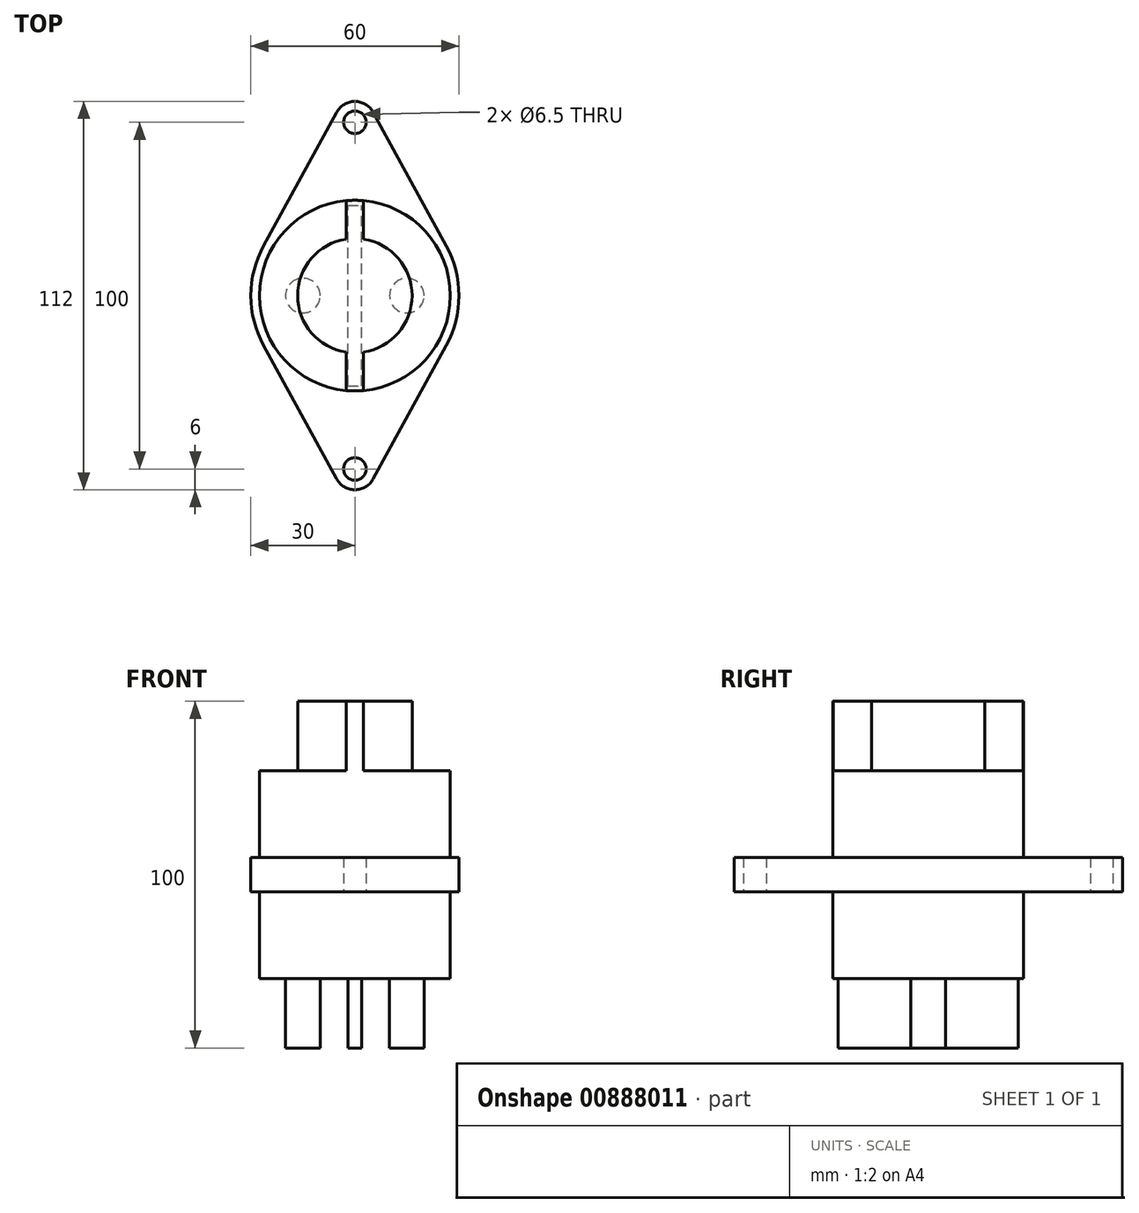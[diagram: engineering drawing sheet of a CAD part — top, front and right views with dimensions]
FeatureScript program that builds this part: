
annotation { "Feature Type Name" : "Feature", "Feature Type Description" : "" }
export const myFeature = defineFeature(function(context is Context, id is Id, definition is map)
    precondition{}
    {
        {
            var Q0;
            Q0=qCreatedBy(makeId("Top.planeOp"),FACE);
            var sketch = newSketch(context, id + "F0", { "sketchPlane" : qUnion([Q0])});
            skCircle(sketch, "E0", {"center": v(0, 0) * mm, "radius": 30 * mm});
            skCircle(sketch, "E1", {"center": v(0, 50) * mm, "radius": 3.25 * mm});
            skCircle(sketch, "E2.MirrorC", {"center": v(0, -50) * mm, "radius": 3.25 * mm});
            skCircle(sketch, "E3", {"center": v(0, 50) * mm, "radius": 6 * mm});
            skCircle(sketch, "E4.MirrorC", {"center": v(0, -50) * mm, "radius": 6 * mm});
            skLineSegment(sketch, "E5", {"start": v(-26.44, 14.18) * mm, "end": v(-5.26, 52.88) * mm});
            skLineSegment(sketch, "E6.MirrorCS", {"start": v(26.44, 14.18) * mm, "end": v(5.26, 52.88) * mm});
            skLineSegment(sketch, "E7.MirrorCS", {"start": v(-26.44, -14.18) * mm, "end": v(-5.26, -52.88) * mm});
            skLineSegment(sketch, "E8.MirrorCS", {"start": v(26.44, -14.18) * mm, "end": v(5.26, -52.88) * mm});
            skSolve(sketch);
        }
        {
            var Q0;
            Q0 = qSketchRegion(id + "F0", true);
            extrude(context, id + "F1", {"entities" : qUnion([Q0]), "endBound" : BoundingType.SYMMETRIC, "depth" : 100 * mm, "offsetDistance" : 25 * mm});
        }
        {
            var Q0;
            Q0=makeQuery(id+"F1.opExtrude","CAP_FACE",FACE,{"disambiguationData":[OSD([sQuery(id+"F0.wireOp",EDGE,"E0"),sQuery(id+"F0.wireOp",EDGE,"E1"),sQuery(id+"F0.wireOp",EDGE,"E2.MirrorC"),sQuery(id+"F0.wireOp",EDGE,"E3"),sQuery(id+"F0.wireOp",EDGE,"E4.MirrorC"),sQuery(id+"F0.wireOp",EDGE,"E5"),sQuery(id+"F0.wireOp",EDGE,"E6.MirrorCS"),sQuery(id+"F0.wireOp",EDGE,"E7.MirrorCS"),sQuery(id+"F0.wireOp",EDGE,"E8.MirrorCS")])],"isStart":false});
            var sketch = newSketch(context, id + "F2", { "sketchPlane" : qUnion([Q0])});
            skCircle(sketch, "E9", {"center": v(0, 0) * mm, "radius": 27.5 * mm});
            skLineSegment(sketch, "E10.bottom", {"start": v(-55.61, 69.95) * mm, "end": v(65.23, 69.95) * mm});
            skLineSegment(sketch, "E10.top", {"start": v(-55.61, -69.95) * mm, "end": v(65.23, -69.95) * mm});
            skLineSegment(sketch, "E10.left", {"start": v(-55.61, 69.95) * mm, "end": v(-55.61, -69.95) * mm});
            skLineSegment(sketch, "E10.right", {"start": v(65.23, 69.95) * mm, "end": v(65.23, -69.95) * mm});
            skSolve(sketch);
        }
        {
            var Q0;
            Q0 = qSketchRegion(id + "F2", true);
            extrude(context, id + "F3", {"entities" : qUnion([Q0]), "operationType" : NewBodyOperationType.REMOVE, "oppositeDirection" : true, "depth" : 45 * mm, "offsetDistance" : 25 * mm});
        }
        {
            var Q0;
            Q0=makeQuery(id+"F1.opExtrude","CAP_FACE",FACE,{"disambiguationData":[OSD([sQuery(id+"F0.wireOp",EDGE,"E0"),sQuery(id+"F0.wireOp",EDGE,"E1"),sQuery(id+"F0.wireOp",EDGE,"E2.MirrorC"),sQuery(id+"F0.wireOp",EDGE,"E3"),sQuery(id+"F0.wireOp",EDGE,"E4.MirrorC"),sQuery(id+"F0.wireOp",EDGE,"E5"),sQuery(id+"F0.wireOp",EDGE,"E6.MirrorCS"),sQuery(id+"F0.wireOp",EDGE,"E7.MirrorCS"),sQuery(id+"F0.wireOp",EDGE,"E8.MirrorCS")])],"isStart":false});
            var sketch = newSketch(context, id + "F4", { "sketchPlane" : qUnion([Q0])});
            skArc(sketch, "E11", {"start": v(-2.5, 38.39) * mm, "mid": v(-38.47, 0) * mm, "end": v(-2.5, -38.39) * mm});
            skArc(sketch, "E12", {"start": v(-2.5, 16.31) * mm, "mid": v(-16.5, 0) * mm, "end": v(-2.5, -16.31) * mm});
            skLineSegment(sketch, "E13.0", {"start": v(-2.5, 38.39) * mm, "end": v(-2.5, 16.31) * mm});
            skLineSegment(sketch, "E14.0", {"start": v(2.5, 38.39) * mm, "end": v(2.5, 16.31) * mm});
            skPoint(sketch, "E15.start.orphan", {"position": v(0, 38.47) * mm});
            skLineSegment(sketch, "E16.MirrorCS", {"start": v(-2.5, -38.39) * mm, "end": v(-2.5, -16.31) * mm});
            skLineSegment(sketch, "E17.MirrorCS", {"start": v(2.5, -38.39) * mm, "end": v(2.5, -16.31) * mm});
            skArc(sketch, "E18.trimOffspring", {"start": v(2.5, -16.31) * mm, "mid": v(16.5, 0) * mm, "end": v(2.5, 16.31) * mm});
            skArc(sketch, "E19.trimOffspring", {"start": v(2.5, -38.39) * mm, "mid": v(38.47, 0) * mm, "end": v(2.5, 38.39) * mm});
            skSolve(sketch);
        }
        {
            var Q0;
            Q0 = qSketchRegion(id + "F4", true);
            extrude(context, id + "F5", {"entities" : qUnion([Q0]), "operationType" : NewBodyOperationType.REMOVE, "oppositeDirection" : true, "depth" : 20 * mm, "offsetDistance" : 25 * mm});
        }
        {
            var Q0;
            Q0=makeQuery(id+"F1.opExtrude","CAP_FACE",FACE,{"disambiguationData":[OSD([sQuery(id+"F0.wireOp",EDGE,"E0"),sQuery(id+"F0.wireOp",EDGE,"E1"),sQuery(id+"F0.wireOp",EDGE,"E2.MirrorC"),sQuery(id+"F0.wireOp",EDGE,"E3"),sQuery(id+"F0.wireOp",EDGE,"E4.MirrorC"),sQuery(id+"F0.wireOp",EDGE,"E5"),sQuery(id+"F0.wireOp",EDGE,"E6.MirrorCS"),sQuery(id+"F0.wireOp",EDGE,"E7.MirrorCS"),sQuery(id+"F0.wireOp",EDGE,"E8.MirrorCS")])],"isStart":false});
            var sketch = newSketch(context, id + "F6", { "sketchPlane" : qUnion([Q0])});
            skCircle(sketch, "E20", {"center": v(0, 0) * mm, "radius": 6 * mm});
            skArc(sketch, "E21", {"start": v(2.5, -22.15) * mm, "mid": v(22.3, 0) * mm, "end": v(2.5, 22.15) * mm});
            skLineSegment(sketch, "E22", {"start": v(-2.5, 22.15) * mm, "end": v(-2.5, 5.45) * mm});
            skLineSegment(sketch, "E23", {"start": v(2.5, 22.15) * mm, "end": v(2.5, 5.45) * mm});
            skLineSegment(sketch, "E24.MirrorCS", {"start": v(-2.5, -22.15) * mm, "end": v(-2.5, -5.45) * mm});
            skLineSegment(sketch, "E25.MirrorCS", {"start": v(2.5, -22.15) * mm, "end": v(2.5, -5.45) * mm});
            skPoint(sketch, "E26.orphan", {"position": v(-2.5, 23.79) * mm});
            skPoint(sketch, "E27.orphan", {"position": v(2.5, 23.71) * mm});
            skPoint(sketch, "E28.orphan", {"position": v(-2.5, -23.79) * mm});
            skPoint(sketch, "E29.orphan", {"position": v(2.5, -23.71) * mm});
            skArc(sketch, "E30.trimOffspring", {"start": v(-2.5, 22.15) * mm, "mid": v(-22.3, 0) * mm, "end": v(-2.5, -22.15) * mm});
            skSolve(sketch);
        }
        {
            var Q0;
            {var subQ0=sQuery(id+"F6.wireOp",EDGE,"E21");Q0=makeQuery(id+"F6.imprint","IMPRINT",FACE,{"disambiguationData":[TD([[makeQuery(id+"F6.imprint","IMPRINT",EDGE,{"derivedFrom":subQ0}),1.0]])]});}
            var Q1;
            {var subQ2=sQuery(id+"F6.wireOp",EDGE,"E30.trimOffspring");Q1=makeQuery(id+"F6.imprint","IMPRINT",FACE,{"disambiguationData":[TD([[makeQuery(id+"F6.imprint","IMPRINT",EDGE,{"derivedFrom":subQ2}),1.0]])]});}
            var Q2;
            {var subQ5=makeQuery(id+"F5.boolean.opBoolean","COPY",EDGE,{"derivedFrom":makeQuery(id+"F5.opExtrude","CAP_EDGE",EDGE,{"disambiguationData":[OSD([sQuery(id+"F4.wireOp",EDGE,"E12")])],"isStart":true})});Q2=makeQuery(id+"F6.imprint","IMPRINT",FACE,{"disambiguationData":[TD([[makeQuery(id+"F6.imprint","IMPRINT",EDGE,{"derivedFrom":subQ5}),1.0]])]});}
            var Q3;
            {var subQ5=makeQuery(id+"F5.boolean.opBoolean","COPY",EDGE,{"derivedFrom":makeQuery(id+"F5.opExtrude","CAP_EDGE",EDGE,{"disambiguationData":[OSD([sQuery(id+"F4.wireOp",EDGE,"E18.trimOffspring")])],"isStart":true})});Q3=makeQuery(id+"F6.imprint","IMPRINT",FACE,{"disambiguationData":[TD([[makeQuery(id+"F6.imprint","IMPRINT",EDGE,{"derivedFrom":subQ5}),1.0]])]});}
            extrude(context, id + "F7", {"entities" : qUnion([Q0, Q1, Q2, Q3]), "operationType" : NewBodyOperationType.REMOVE, "oppositeDirection" : true, "depth" : 10 * mm, "offsetDistance" : 25 * mm});
        }
        {
            var Q0;
            Q0=makeQuery(id+"F1.opExtrude","CAP_FACE",FACE,{"disambiguationData":[OSD([sQuery(id+"F0.wireOp",EDGE,"E0"),sQuery(id+"F0.wireOp",EDGE,"E1"),sQuery(id+"F0.wireOp",EDGE,"E2.MirrorC"),sQuery(id+"F0.wireOp",EDGE,"E3"),sQuery(id+"F0.wireOp",EDGE,"E4.MirrorC"),sQuery(id+"F0.wireOp",EDGE,"E5"),sQuery(id+"F0.wireOp",EDGE,"E6.MirrorCS"),sQuery(id+"F0.wireOp",EDGE,"E7.MirrorCS"),sQuery(id+"F0.wireOp",EDGE,"E8.MirrorCS")])],"isStart":true});
            var sketch = newSketch(context, id + "F8", { "sketchPlane" : qUnion([Q0])});
            skCircle(sketch, "E31", {"center": v(0, 0) * mm, "radius": 27.5 * mm});
            skLineSegment(sketch, "E32.bottom", {"start": v(-55.93, 65.36) * mm, "end": v(69.86, 65.36) * mm});
            skLineSegment(sketch, "E32.top", {"start": v(-55.93, -73.85) * mm, "end": v(69.86, -73.85) * mm});
            skLineSegment(sketch, "E32.left", {"start": v(-55.93, 65.36) * mm, "end": v(-55.93, -73.85) * mm});
            skLineSegment(sketch, "E32.right", {"start": v(69.86, 65.36) * mm, "end": v(69.86, -73.85) * mm});
            skSolve(sketch);
        }
        {
            var Q0;
            Q0=makeQuery(id+"F8.imprint","IMPRINT",FACE,{"disambiguationData":[TD([[makeQuery(id+"F8.imprint","IMPRINT",EDGE,{"derivedFrom":sQuery(id+"F8.wireOp",EDGE,"E31")}),-1.0]])]});
            extrude(context, id + "F9", {"entities" : qUnion([Q0]), "operationType" : NewBodyOperationType.REMOVE, "oppositeDirection" : true, "depth" : 45 * mm, "offsetDistance" : 25 * mm});
        }
        {
            var Q0;
            Q0=makeQuery(id+"F1.opExtrude","CAP_FACE",FACE,{"disambiguationData":[OSD([sQuery(id+"F0.wireOp",EDGE,"E0"),sQuery(id+"F0.wireOp",EDGE,"E1"),sQuery(id+"F0.wireOp",EDGE,"E2.MirrorC"),sQuery(id+"F0.wireOp",EDGE,"E3"),sQuery(id+"F0.wireOp",EDGE,"E4.MirrorC"),sQuery(id+"F0.wireOp",EDGE,"E5"),sQuery(id+"F0.wireOp",EDGE,"E6.MirrorCS"),sQuery(id+"F0.wireOp",EDGE,"E7.MirrorCS"),sQuery(id+"F0.wireOp",EDGE,"E8.MirrorCS")])],"isStart":true});
            var sketch = newSketch(context, id + "F10", { "sketchPlane" : qUnion([Q0])});
            skCircle(sketch, "E33", {"center": v(-15, 0) * mm, "radius": 5 * mm});
            skCircle(sketch, "E34.MirrorC", {"center": v(15, 0) * mm, "radius": 5 * mm});
            skLineSegment(sketch, "E35.bottom", {"start": v(-56.34, 43.1) * mm, "end": v(65.96, 43.1) * mm});
            skLineSegment(sketch, "E35.top", {"start": v(-56.34, -55.07) * mm, "end": v(65.96, -55.07) * mm});
            skLineSegment(sketch, "E35.left", {"start": v(-56.34, 43.1) * mm, "end": v(-56.34, -55.07) * mm});
            skLineSegment(sketch, "E35.right", {"start": v(65.96, 43.1) * mm, "end": v(65.96, -55.07) * mm});
            skSolve(sketch);
        }
        {
            var Q0;
            Q0=makeQuery(id+"F10.imprint","IMPRINT",FACE,{"disambiguationData":[TD([[makeQuery(id+"F10.imprint","IMPRINT",EDGE,{"derivedFrom":sQuery(id+"F10.wireOp",EDGE,"E33")}),-1.0]])]});
            extrude(context, id + "F11", {"entities" : qUnion([Q0]), "operationType" : NewBodyOperationType.REMOVE, "oppositeDirection" : true, "depth" : 20 * mm, "offsetDistance" : 25 * mm});
        }
        {
            var Q0;
            Q0=makeQuery(id+"F11.boolean.opBoolean","COPY",FACE,{"derivedFrom":makeQuery(id+"F11.opExtrude","CAP_FACE",FACE,{"disambiguationData":[OSD([sQuery(id+"F8.wireOp",EDGE,"E31"),sQuery(id+"F10.wireOp",EDGE,"E33"),sQuery(id+"F10.wireOp",EDGE,"E34.MirrorC")])],"isStart":false})});
            var sketch = newSketch(context, id + "F12", { "sketchPlane" : qUnion([Q0])});
            skLineSegment(sketch, "E36.bottom", {"start": v(-2, 26) * mm, "end": v(2, 26) * mm});
            skLineSegment(sketch, "E36.top", {"start": v(-2, -26) * mm, "end": v(2, -26) * mm});
            skLineSegment(sketch, "E36.left", {"start": v(-2, 26) * mm, "end": v(-2, -26) * mm});
            skLineSegment(sketch, "E36.right", {"start": v(2, 26) * mm, "end": v(2, -26) * mm});
            skPoint(sketch, "E36.middle", {"position": v(0, 0) * mm});
            skSolve(sketch);
        }
        {
            var Q0;
            Q0 = qSketchRegion(id + "F12", true);
            extrude(context, id + "F13", {"entities" : qUnion([Q0]), "operationType" : NewBodyOperationType.ADD, "depth" : 20 * mm, "offsetDistance" : 25 * mm});
        }
    });
